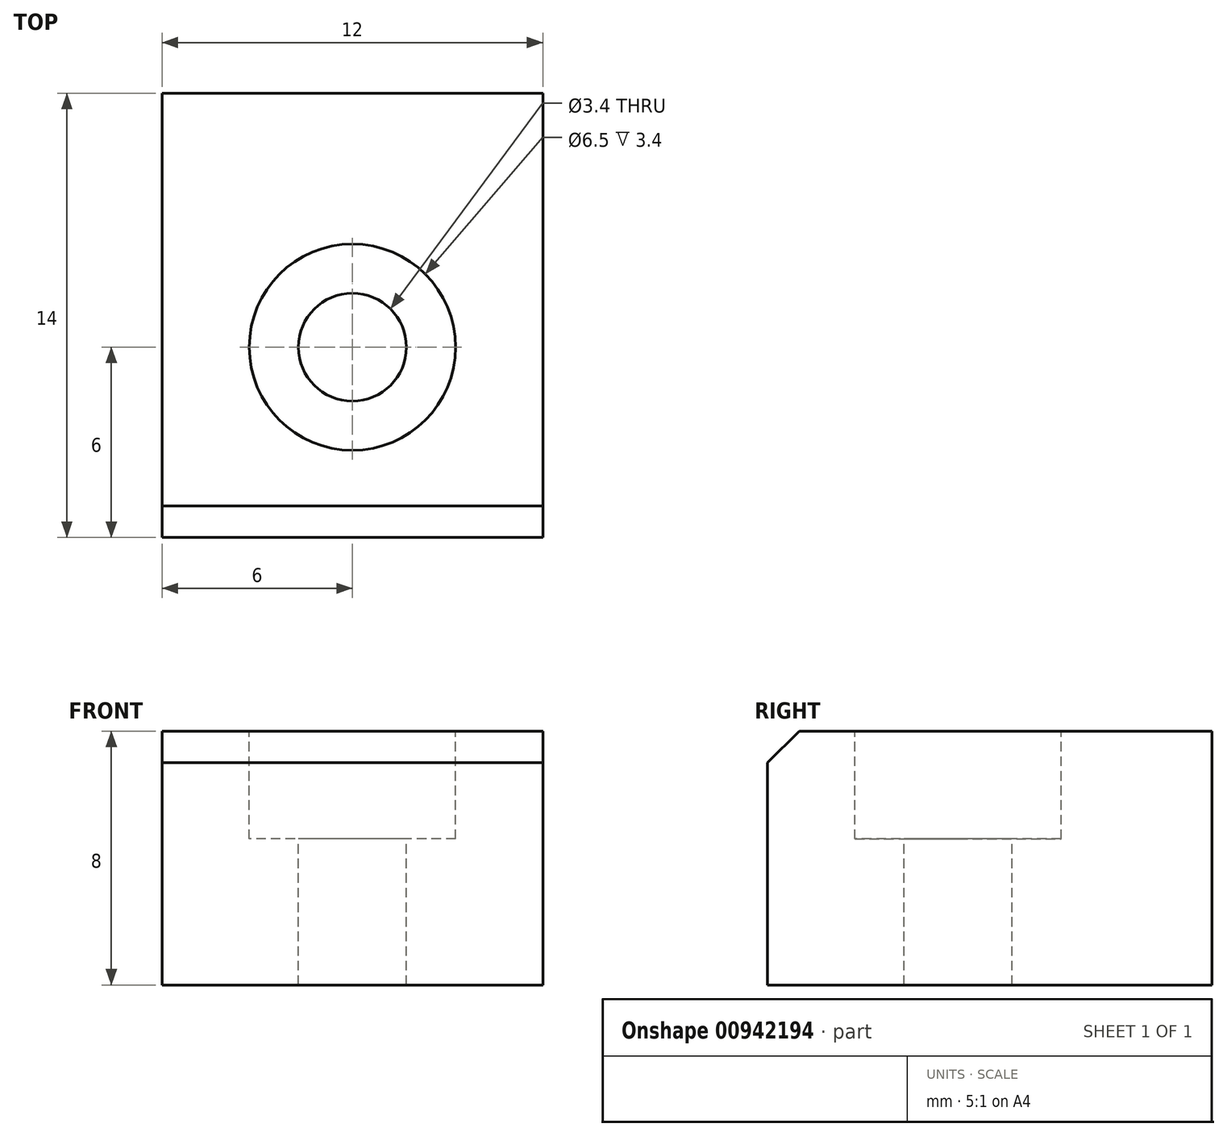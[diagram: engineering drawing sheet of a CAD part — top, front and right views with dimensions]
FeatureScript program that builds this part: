
annotation { "Feature Type Name" : "Feature", "Feature Type Description" : "" }
export const myFeature = defineFeature(function(context is Context, id is Id, definition is map)
    precondition{}
    {
        {
            var Q0;
            Q0=qCreatedBy(makeId("Top.planeOp"),FACE);
            var sketch = newSketch(context, id + "F0", { "sketchPlane" : qUnion([Q0])});
            skLineSegment(sketch, "E0.bottom", {"start": v(6, -7) * mm, "end": v(-6, -7) * mm});
            skLineSegment(sketch, "E0.top", {"start": v(6, 7) * mm, "end": v(-6, 7) * mm});
            skLineSegment(sketch, "E0.left", {"start": v(6, -7) * mm, "end": v(6, 7) * mm});
            skLineSegment(sketch, "E0.right", {"start": v(-6, -7) * mm, "end": v(-6, 7) * mm});
            skPoint(sketch, "E0.middle", {"position": v(0, 0) * mm});
            skSolve(sketch);
        }
        {
            var Q0;
            Q0=makeQuery(id+"F0.imprint","IMPRINT",FACE,{"disambiguationData":[TD([[makeQuery(id+"F0.imprint","IMPRINT",EDGE,{"derivedFrom":sQuery(id+"F0.wireOp",EDGE,"E0.bottom")}),-1.0]])]});
            extrude(context, id + "F1", {"entities" : qUnion([Q0]), "depth" : 8 * mm, "offsetDistance" : 25 * mm});
        }
        {
            var Q0;
            Q0=makeQuery(id+"F1.opExtrude","CAP_EDGE",EDGE,{"disambiguationData":[OSD([sQuery(id+"F0.wireOp",EDGE,"E0.bottom")])],"isStart":false});
            chamfer(context, id + "F2", {"entities" : qUnion([Q0]), "width" : 1 * mm, "tangentPropagation" : true});
        }
        {
            var Q0;
            Q0=makeQuery(id+"F1.opExtrude","CAP_FACE",FACE,{"disambiguationData":[OSD([sQuery(id+"F0.wireOp",EDGE,"E0.bottom"),sQuery(id+"F0.wireOp",EDGE,"E0.top"),sQuery(id+"F0.wireOp",EDGE,"E0.left"),sQuery(id+"F0.wireOp",EDGE,"E0.right")])],"isStart":false});
            var sketch = newSketch(context, id + "F3", { "sketchPlane" : qUnion([Q0])});
            skPoint(sketch, "E1", {"position": v(0, -1) * mm});
            skSolve(sketch);
        }
        {
            var Q0;
            Q0=sQuery(id+"F3.wireOp",VERTEX,"E1");
            var Q1;
            Q1=makeQuery(id+"F1.opExtrude","SWEPT_BODY",BODY,{"disambiguationData":[OSD([sQuery(id+"F0.wireOp",EDGE,"E0.bottom"),sQuery(id+"F0.wireOp",EDGE,"E0.top"),sQuery(id+"F0.wireOp",EDGE,"E0.left"),sQuery(id+"F0.wireOp",EDGE,"E0.right")])]});
            hole(context, id + "F4", {"style" : HoleStyle.C_BORE, "endStyle" : HoleEndStyle.BLIND, "holeDiameter" : 3.4 * mm, "cBoreDiameter" : 6.5 * mm, "cBoreDepth" : 3.4 * mm, "majorDiameter" : 5 * mm, "holeDepth" : 10 * mm, "isTappedThrough" : true, "tappedDepth" : 8.5 * mm, "tapClearance" : 3, "startFromSketch" : true, "locations" : qUnion([Q0]), "scope" : qUnion([Q1])});
        }
    });
